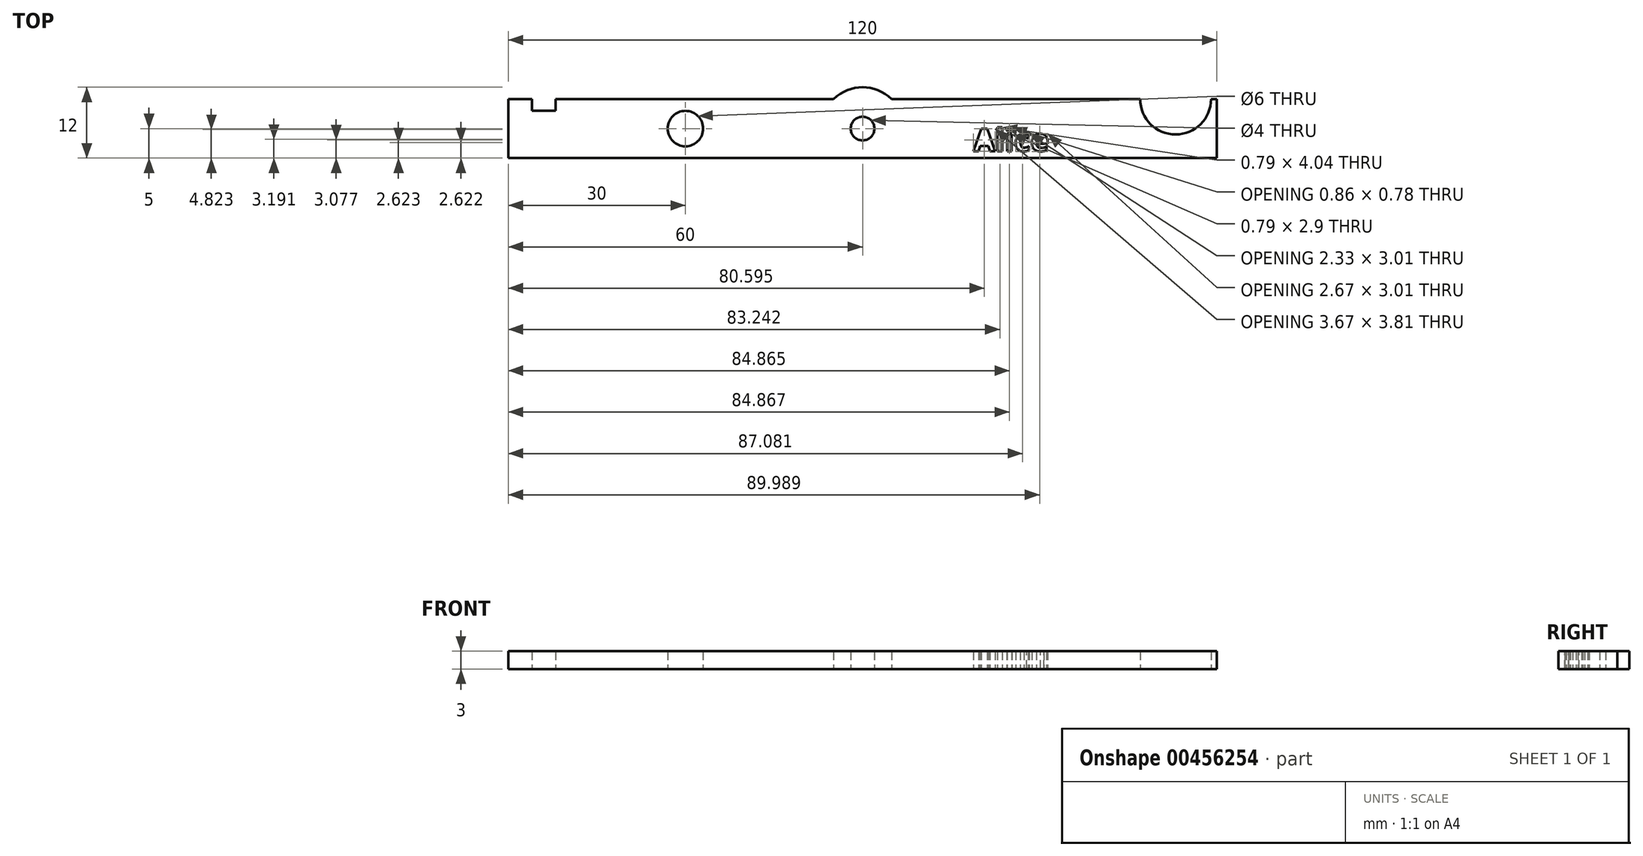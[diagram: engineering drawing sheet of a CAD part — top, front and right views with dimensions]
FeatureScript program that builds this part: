
annotation { "Feature Type Name" : "Feature", "Feature Type Description" : "" }
export const myFeature = defineFeature(function(context is Context, id is Id, definition is map)
    precondition{}
    {
        {
            var Q0;
            Q0=qCreatedBy(makeId("Top.planeOp"),FACE);
            var sketch = newSketch(context, id + "F0", { "sketchPlane" : qUnion([Q0])});
            skLineSegment(sketch, "E0.bottom", {"start": v(-60, -5) * mm, "end": v(60, -5) * mm});
            skLineSegment(sketch, "E0.top", {"start": v(-60, 5) * mm, "end": v(60, 5) * mm});
            skLineSegment(sketch, "E0.left", {"start": v(-60, -5) * mm, "end": v(-60, 5) * mm});
            skLineSegment(sketch, "E0.right", {"start": v(60, -5) * mm, "end": v(60, 5) * mm});
            skPoint(sketch, "E0.middle", {"position": v(0, 0) * mm});
            skLineSegment(sketch, "E1.bottom", {"start": v(-52, 5) * mm, "end": v(-56, 5) * mm});
            skLineSegment(sketch, "E1.top", {"start": v(-52, 3) * mm, "end": v(-56, 3) * mm});
            skLineSegment(sketch, "E1.left", {"start": v(-52, 5) * mm, "end": v(-52, 3) * mm});
            skLineSegment(sketch, "E1.right", {"start": v(-56, 5) * mm, "end": v(-56, 3) * mm});
            skCircle(sketch, "E2", {"center": v(0, 0) * mm, "radius": 2 * mm});
            skCircle(sketch, "E3", {"center": v(0, 0) * mm, "radius": 7 * mm});
            skCircle(sketch, "E4", {"center": v(-30, 0) * mm, "radius": 3 * mm});
            skCircle(sketch, "E5", {"center": v(53, 5) * mm, "radius": 6 * mm});
            skText(sketch, "E6", { "text": "Alice", "fontName": "OpenSans-Bold.ttf"});
            const initialGuessF0  = {"E6": [0.01876, -0.00383, 1, 0, 0.00383]};
            skSetInitialGuess(sketch, initialGuessF0);
            skSolve(sketch);
        }
        {
            var Q0;
            {var subQ0=sQuery(id+"F0.wireOp",EDGE,"E0.left");Q0=makeQuery(id+"F0.imprint","IMPRINT",FACE,{"disambiguationData":[TD([[makeQuery(id+"F0.imprint","IMPRINT",EDGE,{"derivedFrom":subQ0}),-1.0]])]});}
            var Q1;
            {var subQ0=sQuery(id+"F0.wireOp",EDGE,"E0.right");Q1=makeQuery(id+"F0.imprint","IMPRINT",FACE,{"disambiguationData":[TD([[makeQuery(id+"F0.imprint","IMPRINT",EDGE,{"derivedFrom":subQ0}),1.0]])]});}
            var Q2;
            {var subQ0=sQuery(id+"F0.wireOp",EDGE,"E3");var subQ1=sQuery(id+"F0.wireOp",EDGE,"E0.bottom");var subQ2=makeQuery(id+"F0.imprint","INTERSECT",VERTEX,{"disambiguationData":[OD(0.0)],"derivedFrom":[subQ1,subQ0]});Q2=makeQuery(id+"F0.imprint","IMPRINT",FACE,{"disambiguationData":[TD([[makeQuery(id+"F0.imprint","IMPRINT",EDGE,{"disambiguationData":[TD([[subQ2,-1.0]])],"derivedFrom":subQ1}),-1.0]])]});}
            var Q3;
            Q3=makeQuery(id+"F0.imprint","IMPRINT",FACE,{"disambiguationData":[TD([[makeQuery(id+"F0.imprint","IMPRINT",EDGE,{"derivedFrom":sQuery(id+"F0.wireOp",EDGE,"E2")}),-1.0]])]});
            var Q4;
            {var subQ0=sQuery(id+"F0.wireOp",EDGE,"E3");var subQ1=sQuery(id+"F0.wireOp",EDGE,"E0.top");var subQ2=makeQuery(id+"F0.imprint","INTERSECT",VERTEX,{"disambiguationData":[OD(0.0)],"derivedFrom":[subQ1,subQ0]});Q4=makeQuery(id+"F0.imprint","IMPRINT",FACE,{"disambiguationData":[TD([[makeQuery(id+"F0.imprint","IMPRINT",EDGE,{"disambiguationData":[TD([[subQ2,-1.0]])],"derivedFrom":subQ1}),1.0]])]});}
            extrude(context, id + "F1", {"entities" : qUnion([Q0, Q1, Q2, Q3, Q4]), "depth" : 3 * mm});
        }
    });
